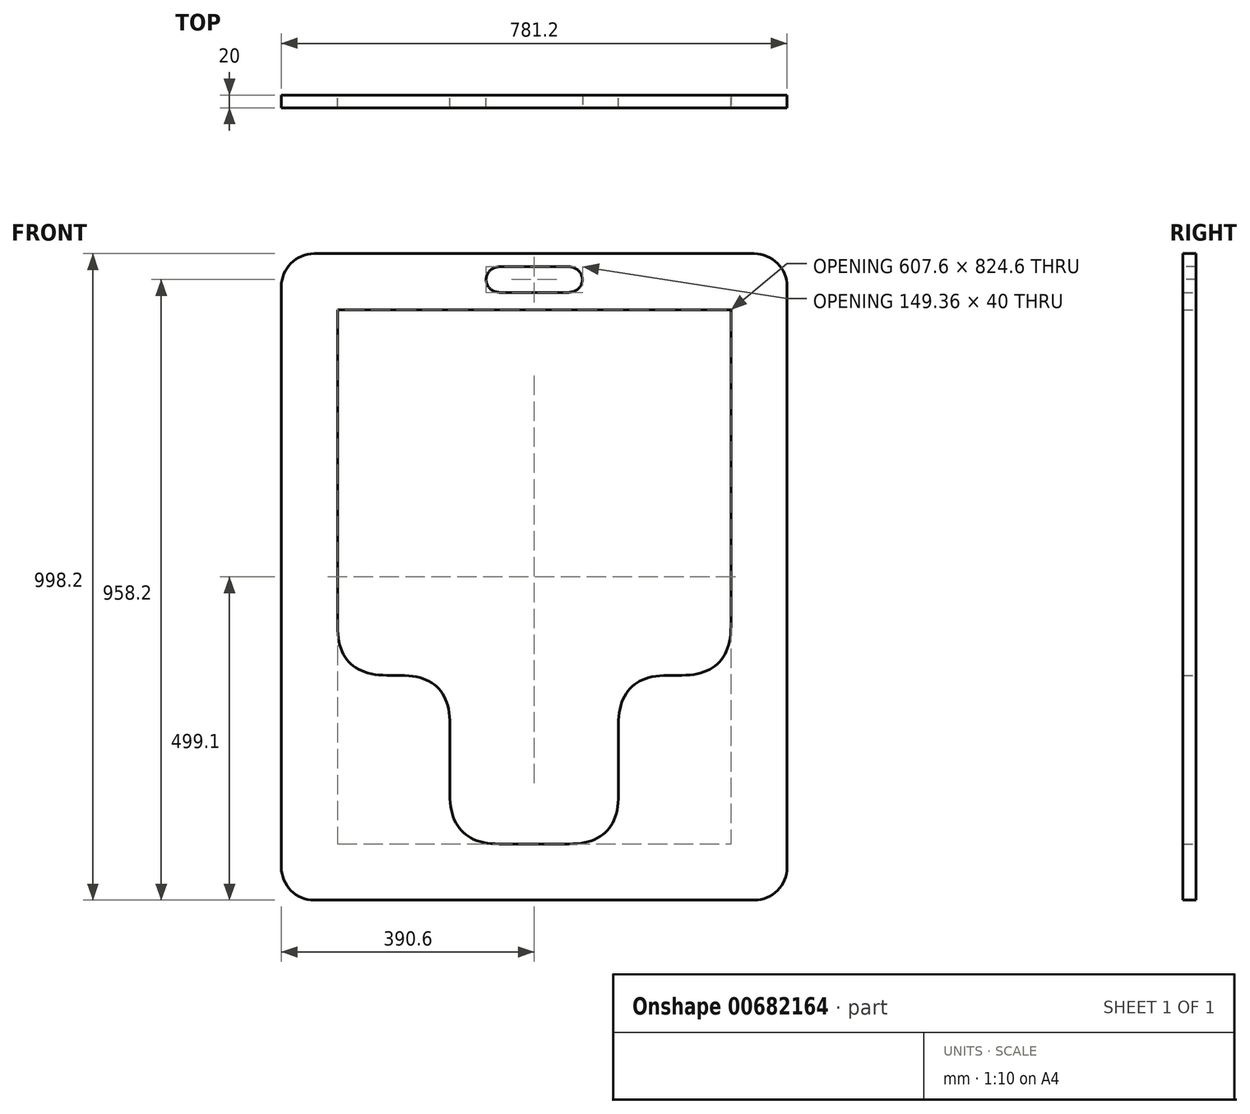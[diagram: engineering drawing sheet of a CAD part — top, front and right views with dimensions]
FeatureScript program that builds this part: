
annotation { "Feature Type Name" : "Feature", "Feature Type Description" : "" }
export const myFeature = defineFeature(function(context is Context, id is Id, definition is map)
    precondition{}
    {
        {
            var Q0;
            Q0=qCreatedBy(makeId("Front.planeOp"),FACE);
            var sketch = newSketch(context, id + "F0", { "sketchPlane" : qUnion([Q0])});
            skLineSegment(sketch, "E0.bottom", {"start": v(-390.6, 499.1) * mm, "end": v(390.6, 499.1) * mm});
            skLineSegment(sketch, "E0.top", {"start": v(-390.6, -499.1) * mm, "end": v(390.6, -499.1) * mm});
            skLineSegment(sketch, "E0.left", {"start": v(-390.6, 499.1) * mm, "end": v(-390.6, -499.1) * mm});
            skLineSegment(sketch, "E0.right", {"start": v(390.6, 499.1) * mm, "end": v(390.6, -499.1) * mm});
            skPoint(sketch, "E0.middle", {"position": v(0, 0) * mm});
            skSolve(sketch);
        }
        {
            var Q0;
            Q0=makeQuery(id+"F0.imprint","IMPRINT",FACE,{"disambiguationData":[TD([[makeQuery(id+"F0.imprint","IMPRINT",EDGE,{"derivedFrom":sQuery(id+"F0.wireOp",EDGE,"E0.bottom")}),-1.0]])]});
            extrude(context, id + "F1", {"entities" : qUnion([Q0]), "depth" : 20 * mm, "offsetDistance" : 25.4 * mm});
        }
        {
            var Q0;
            Q0=makeQuery(id+"F1.opExtrude","SWEPT_EDGE",EDGE,{"disambiguationData":[OSD([sQuery(id+"F0.wireOp",EDGE,"E0.bottom"),sQuery(id+"F0.wireOp",EDGE,"E0.left")])]});
            var Q1;
            Q1=makeQuery(id+"F1.opExtrude","SWEPT_EDGE",EDGE,{"disambiguationData":[OSD([sQuery(id+"F0.wireOp",EDGE,"E0.bottom"),sQuery(id+"F0.wireOp",EDGE,"E0.right")])]});
            var Q2;
            Q2=makeQuery(id+"F1.opExtrude","SWEPT_EDGE",EDGE,{"disambiguationData":[OSD([sQuery(id+"F0.wireOp",EDGE,"E0.top"),sQuery(id+"F0.wireOp",EDGE,"E0.right")])]});
            var Q3;
            Q3=makeQuery(id+"F1.opExtrude","SWEPT_EDGE",EDGE,{"disambiguationData":[OSD([sQuery(id+"F0.wireOp",EDGE,"E0.top"),sQuery(id+"F0.wireOp",EDGE,"E0.left")])]});
            fillet(context, id + "F2", {"entities" : qUnion([Q0, Q1, Q2, Q3]), "radius" : 50.8 * mm, "tangentPropagation" : true, "allowEdgeOverflow" : false});
        }
        {
            var Q0;
            Q0=qCreatedBy(makeId("Front.planeOp"),FACE);
            var sketch = newSketch(context, id + "F3", { "sketchPlane" : qUnion([Q0])});
            skLineSegment(sketch, "E1", {"start": v(-303.8, 412.3) * mm, "end": v(-303.8, -151.9) * mm});
            skLineSegment(sketch, "E2", {"start": v(-303.8, -151.9) * mm, "end": v(-130.2, -151.9) * mm});
            skLineSegment(sketch, "E3", {"start": v(-130.2, -151.9) * mm, "end": v(-130.2, -412.3) * mm});
            skLineSegment(sketch, "E4", {"start": v(-130.2, -412.3) * mm, "end": v(130.2, -412.3) * mm});
            skLineSegment(sketch, "E5", {"start": v(130.2, -412.3) * mm, "end": v(130.2, -151.9) * mm});
            skLineSegment(sketch, "E6", {"start": v(130.2, -151.9) * mm, "end": v(303.8, -151.9) * mm});
            skLineSegment(sketch, "E7", {"start": v(303.8, -151.9) * mm, "end": v(303.8, 412.3) * mm});
            skLineSegment(sketch, "E8", {"start": v(303.8, 412.3) * mm, "end": v(-303.8, 412.3) * mm});
            skSolve(sketch);
        }
        {
            var Q0;
            Q0 = qSketchRegion(id + "F3", true);
            extrude(context, id + "F4", {"entities" : qUnion([Q0]), "operationType" : NewBodyOperationType.REMOVE, "depth" : 25.4 * mm, "offsetDistance" : 25.4 * mm});
        }
        {
            var Q0;
            Q0=makeQuery(id+"F4.boolean.opBoolean","COPY",EDGE,{"derivedFrom":makeQuery(id+"F4.opExtrude","SWEPT_EDGE",EDGE,{"disambiguationData":[OSD([sQuery(id+"F3.wireOp",EDGE,"E1"),sQuery(id+"F3.wireOp",EDGE,"E2")])]})});
            var Q1;
            Q1=makeQuery(id+"F4.boolean.opBoolean","COPY",EDGE,{"derivedFrom":makeQuery(id+"F4.opExtrude","SWEPT_EDGE",EDGE,{"disambiguationData":[OSD([sQuery(id+"F3.wireOp",EDGE,"E2"),sQuery(id+"F3.wireOp",EDGE,"E3")])]})});
            var Q2;
            Q2=makeQuery(id+"F4.boolean.opBoolean","COPY",EDGE,{"derivedFrom":makeQuery(id+"F4.opExtrude","SWEPT_EDGE",EDGE,{"disambiguationData":[OSD([sQuery(id+"F3.wireOp",EDGE,"E3"),sQuery(id+"F3.wireOp",EDGE,"E4")])]})});
            var Q3;
            Q3=makeQuery(id+"F4.boolean.opBoolean","COPY",EDGE,{"derivedFrom":makeQuery(id+"F4.opExtrude","SWEPT_EDGE",EDGE,{"disambiguationData":[OSD([sQuery(id+"F3.wireOp",EDGE,"E5"),sQuery(id+"F3.wireOp",EDGE,"E6")])]})});
            var Q4;
            Q4=makeQuery(id+"F4.boolean.opBoolean","COPY",EDGE,{"derivedFrom":makeQuery(id+"F4.opExtrude","SWEPT_EDGE",EDGE,{"disambiguationData":[OSD([sQuery(id+"F3.wireOp",EDGE,"E6"),sQuery(id+"F3.wireOp",EDGE,"E7")])]})});
            var Q5;
            Q5=makeQuery(id+"F4.boolean.opBoolean","COPY",EDGE,{"derivedFrom":makeQuery(id+"F4.opExtrude","SWEPT_EDGE",EDGE,{"disambiguationData":[OSD([sQuery(id+"F3.wireOp",EDGE,"E4"),sQuery(id+"F3.wireOp",EDGE,"E5")])]})});
            fillet(context, id + "F5", {"entities" : qUnion([Q0, Q1, Q2, Q3, Q4, Q5]), "radius" : 76.2 * mm, "tangentPropagation" : true, "rho" : .5, "crossSection" : FilletCrossSection.CONIC, "allowEdgeOverflow" : false});
        }
        {
            var Q0;
            Q0=qCreatedBy(makeId("Front.planeOp"),FACE);
            var sketch = newSketch(context, id + "F6", { "sketchPlane" : qUnion([Q0])});
            skLineSegment(sketch, "E9.bottom", {"start": v(-130.2, 479.1) * mm, "end": v(130.2, 479.1) * mm});
            skLineSegment(sketch, "E9.top", {"start": v(-130.2, 432.3) * mm, "end": v(130.2, 432.3) * mm});
            skLineSegment(sketch, "E9.left", {"start": v(-130.2, 479.1) * mm, "end": v(-130.2, 432.3) * mm});
            skLineSegment(sketch, "E9.right", {"start": v(130.2, 479.1) * mm, "end": v(130.2, 432.3) * mm});
            skSolve(sketch);
        }
        {
            var Q0;
            Q0 = qSketchRegion(id + "F6", true);
            extrude(context, id + "F7", {"entities" : qUnion([Q0]), "operationType" : NewBodyOperationType.REMOVE, "oppositeDirection" : true, "depth" : 25.4 * mm, "offsetDistance" : 25.4 * mm});
        }
        {
            var Q0;
            Q0=makeQuery(id+"F1.opExtrude","CAP_FACE",FACE,{"disambiguationData":[OSD([sQuery(id+"F0.wireOp",EDGE,"E0.bottom"),sQuery(id+"F0.wireOp",EDGE,"E0.top"),sQuery(id+"F0.wireOp",EDGE,"E0.left"),sQuery(id+"F0.wireOp",EDGE,"E0.right")])],"isStart":false});
            var sketch = newSketch(context, id + "F8", { "sketchPlane" : qUnion([Q0])});
            skLineSegment(sketch, "E10.bottom", {"start": v(-75, 479.1) * mm, "end": v(75, 479.1) * mm});
            skLineSegment(sketch, "E10.top", {"start": v(-75, 439.1) * mm, "end": v(75, 439.1) * mm});
            skLineSegment(sketch, "E10.left", {"start": v(-75, 479.1) * mm, "end": v(-75, 439.1) * mm});
            skLineSegment(sketch, "E10.right", {"start": v(75, 479.1) * mm, "end": v(75, 439.1) * mm});
            skSolve(sketch);
        }
        {
            var Q0;
            Q0 = qSketchRegion(id + "F8", true);
            extrude(context, id + "F9", {"entities" : qUnion([Q0]), "operationType" : NewBodyOperationType.REMOVE, "endBound" : BoundingType.THROUGH_ALL, "oppositeDirection" : true, "depth" : 25.4 * mm, "offsetDistance" : 25.4 * mm});
        }
        {
            var Q0;
            Q0=makeQuery(id+"F9.boolean.opBoolean","COPY",EDGE,{"derivedFrom":makeQuery(id+"F9.opExtrude","SWEPT_EDGE",EDGE,{"disambiguationData":[OSD([sQuery(id+"F8.wireOp",EDGE,"E10.bottom"),sQuery(id+"F8.wireOp",EDGE,"E10.left")])]})});
            var Q1;
            Q1=makeQuery(id+"F9.boolean.opBoolean","COPY",EDGE,{"derivedFrom":makeQuery(id+"F9.opExtrude","SWEPT_EDGE",EDGE,{"disambiguationData":[OSD([sQuery(id+"F8.wireOp",EDGE,"E10.top"),sQuery(id+"F8.wireOp",EDGE,"E10.left")])]})});
            var Q2;
            Q2=makeQuery(id+"F9.boolean.opBoolean","COPY",EDGE,{"derivedFrom":makeQuery(id+"F9.opExtrude","SWEPT_EDGE",EDGE,{"disambiguationData":[OSD([sQuery(id+"F8.wireOp",EDGE,"E10.bottom"),sQuery(id+"F8.wireOp",EDGE,"E10.right")])]})});
            var Q3;
            Q3=makeQuery(id+"F9.boolean.opBoolean","COPY",EDGE,{"derivedFrom":makeQuery(id+"F9.opExtrude","SWEPT_EDGE",EDGE,{"disambiguationData":[OSD([sQuery(id+"F8.wireOp",EDGE,"E10.top"),sQuery(id+"F8.wireOp",EDGE,"E10.right")])]})});
            fillet(context, id + "F10", {"entities" : qUnion([Q0, Q1, Q2, Q3]), "radius" : 25.4 * mm, "tangentPropagation" : true, "rho" : 0.5, "crossSection" : FilletCrossSection.CONIC, "allowEdgeOverflow" : false});
        }
    });
